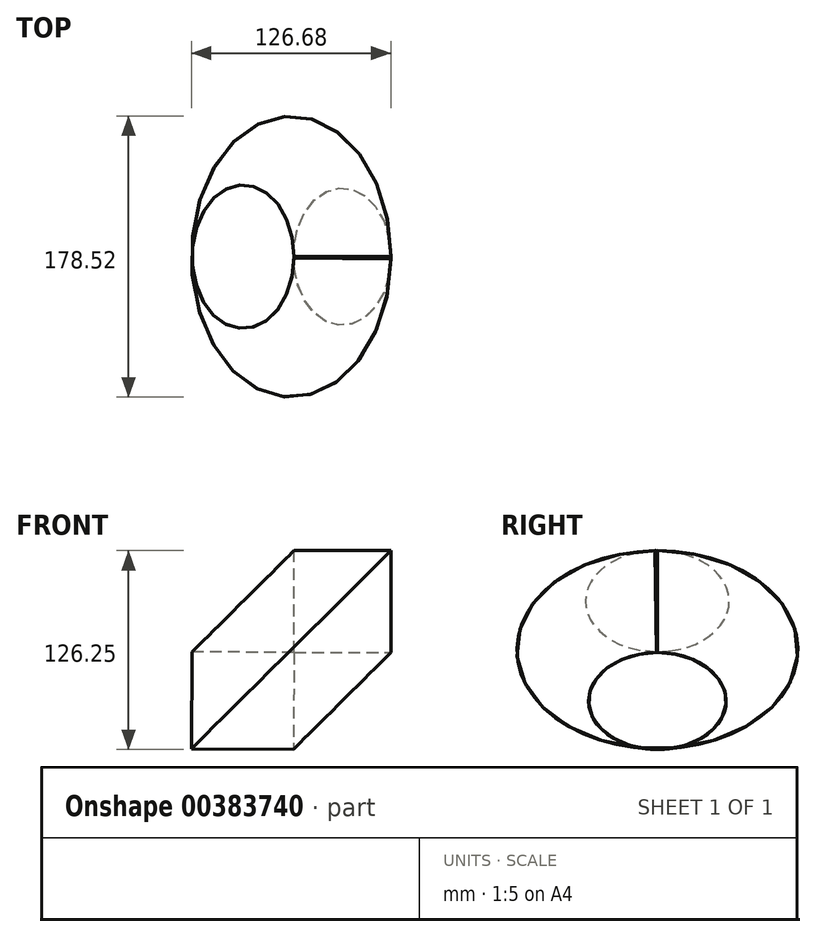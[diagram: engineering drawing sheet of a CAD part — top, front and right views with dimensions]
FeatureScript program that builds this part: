
annotation { "Feature Type Name" : "Feature", "Feature Type Description" : "" }
export const myFeature = defineFeature(function(context is Context, id is Id, definition is map)
    precondition{}
    {
        {
            var Q0;
            Q0=qCreatedBy(makeId("Front.planeOp"),FACE);
            var sketch = newSketch(context, id + "F0", { "sketchPlane" : qUnion([Q0])});
            skLineSegment(sketch, "E0.bottom", {"start": v(0, 0) * mm, "end": v(61.53, 0) * mm});
            skLineSegment(sketch, "E0.top", {"start": v(0, 64.72) * mm, "end": v(61.53, 64.72) * mm});
            skLineSegment(sketch, "E0.left", {"start": v(0, 0) * mm, "end": v(0, 64.72) * mm});
            skLineSegment(sketch, "E0.right", {"start": v(61.53, 0) * mm, "end": v(61.53, 64.72) * mm});
            skPoint(sketch, "E0.middle", {"position": v(30.77, 32.36) * mm});
            skSolve(sketch);
        }
        {
            var Q0;
            Q0=qCreatedBy(makeId("Front.planeOp"),FACE);
            var sketch = newSketch(context, id + "F1", { "sketchPlane" : qUnion([Q0])});
            skLineSegment(sketch, "E1", {"start": v(49.83, -50.18) * mm, "end": v(-49.83, 50.18) * mm, "construction": true});
            skSolve(sketch);
        }
        {
            var Q0;
            Q0=makeQuery(id+"F0.imprint","IMPRINT",FACE,{"disambiguationData":[TD([[makeQuery(id+"F0.imprint","IMPRINT",EDGE,{"derivedFrom":sQuery(id+"F0.wireOp",EDGE,"E0.bottom")}),1.0]])]});
            var Q1;
            Q1=sQuery(id+"F1.wireOp",EDGE,"E1");
            revolve(context, id + "F2", {"entities" : qUnion([Q0]), "axis" : qUnion([Q1]), "revolveType" : RevolveType.ONE_DIRECTION, "angle" : 359 * degree});
        }
    });
